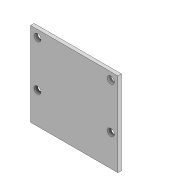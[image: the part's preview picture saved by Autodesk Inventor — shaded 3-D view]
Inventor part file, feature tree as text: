
AUTODESK INVENTOR PART (.ipt)
format: ipt  version: 2022 (Build 260153000, 153)  size: 134,144 bytes
history: native  units: mm
features: extrude x5, sketch x5
ambient origin geometry x8: Origin, YZ Plane, XZ Plane, XY Plane, X Axis, Y Axis, Z Axis, Center Point
bodies: Solid1 (feature_tree)
feature tree (10):
  extrude  "Extrusion1"  Depth=25.0mm
  extrude  "Extrusion2"  Depth=11.0mm
  extrude  "Extrusion3"  Depth=4.5mm
  extrude  "Extrusion4"  Depth=9.0mm
  extrude  "Extrusion5"  Depth=8.5mm
  sketch  "Sketch1"  dims[d0=24.0mm d1=25.0mm]
  sketch  "Sketch2"  dims[d2=1.0mm d3=0.0mm d4=11.0mm]
  sketch  "Sketch3"  dims[d5=11.0mm d6=4.5mm]
  sketch  "Sketch4"  dims[d7=5.0mm d8=0.0mm d9=9.0mm]
  sketch  "Sketch5"  dims[d10=8.0mm d11=0.0mm d12=8.5mm d13=4.0mm d14=2.0mm d15=7.0mm d16=1.5mm d17=0.0mm d19=15.0mm d20=1.0mm d21=1.0mm d22=2.0mm d23=2.0mm d24=2.0mm d25=2.0mm d26=0.0mm d27=0.0mm]
